# Revit family: NU-140 Vertical Airflow Workstation
name_source: partatom
category: Mechanical Equipment
revit_build: Autodesk Revit 2018 (Build: 20180423_1000(x64)
units: mm (PartAtom-declared; Revit-internal decimal feet)

## family parameters
Always vertical = Yes
Cut with Voids When Loaded = No
OmniClass Number = 23.75.00.00
OmniClass Title = Climate Control (HVAC)
Part Type = Normal
Room Calculation Point = No
Round Connector Dimension = Use Diameter
Shared = No
Work Plane-Based = No

## types (4) — shared parameters
DEPTH = 2' - 8"
Manufacturer = Nuaire inc.
WORKZONE DEPTH = 2' - 3"

## per-type parameters (varying)
| type | Model | WIDTH | WORKZONE WIDTH |
| NU-140-330 | NU-140-330 VERTICAL AIRFLOW WORKSTATION | 3' - 2" | 2' - 10" |
| NU-140-430 | NU-140-430 VERTICAL AIRFLOW WORKSTATION | 4' - 2" | 3' - 10" |
| NU-140-530 | NU-140-530 VERTICAL AIRFLOW WORKSTATION | 5' - 2" | 4' - 10" |
| NU-140-630 | NU-140-630 VERTICAL AIRFLOW WORKSTATION | 6' - 2" | 5' - 10" |

## geometry (parser evidence)
native form markers: Sweep x2
no freeform markers — native parametric forms only
